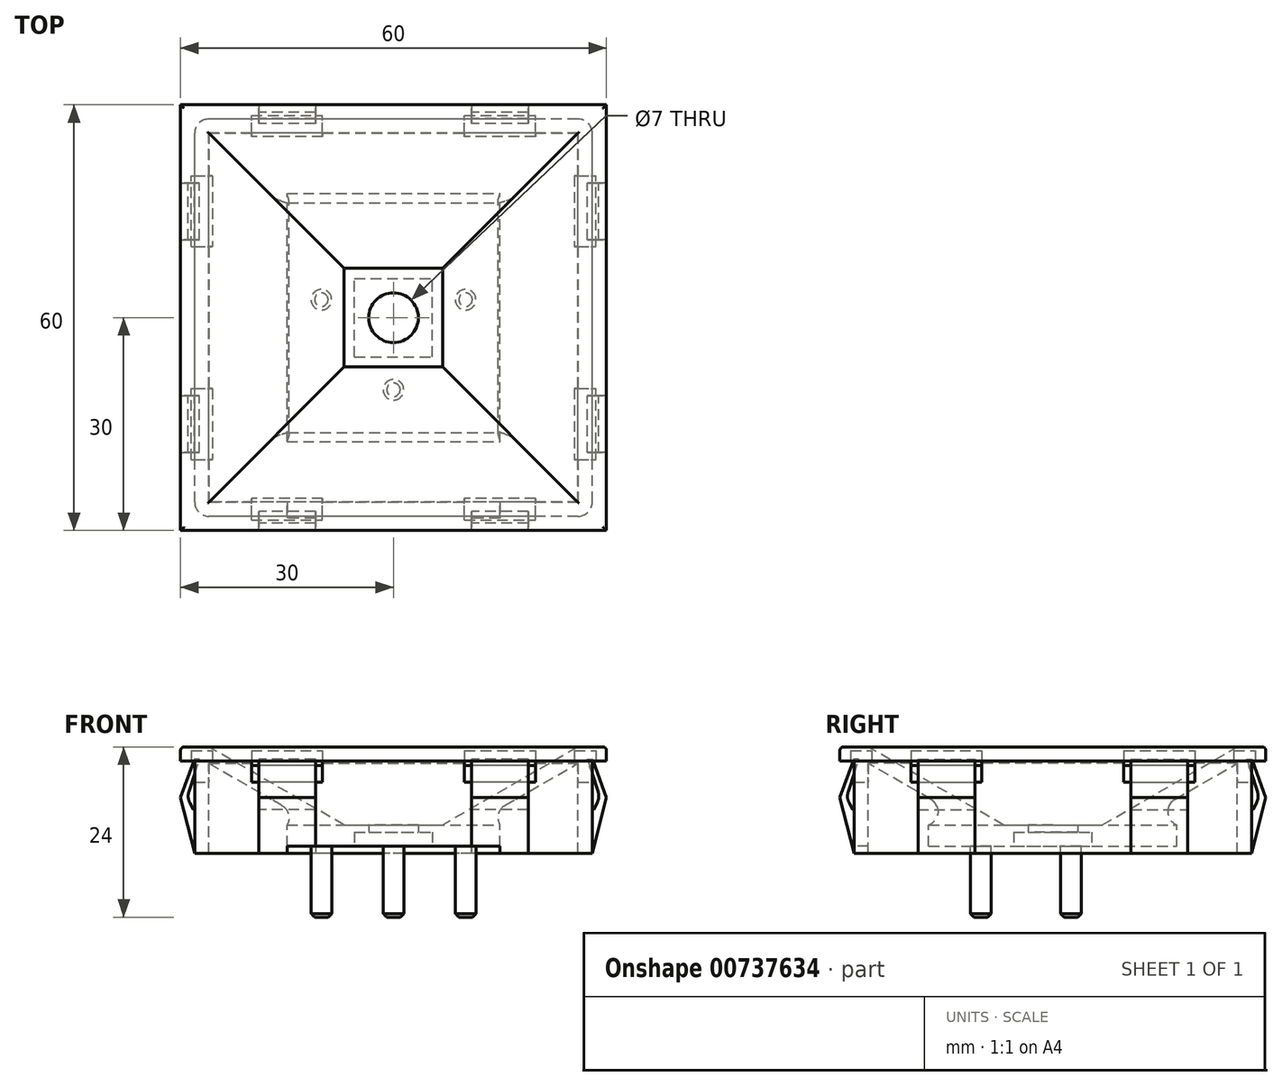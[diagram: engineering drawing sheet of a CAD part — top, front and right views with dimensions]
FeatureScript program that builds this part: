
annotation { "Feature Type Name" : "Feature", "Feature Type Description" : "" }
export const myFeature = defineFeature(function(context is Context, id is Id, definition is map)
    precondition{}
    {
        {
            var Q0;
            Q0=qCreatedBy(makeId("Top.planeOp"),FACE);
            var sketch = newSketch(context, id + "F0", { "sketchPlane" : qUnion([Q0])});
            skLineSegment(sketch, "E0.bottom", {"start": v(30, -30) * mm, "end": v(-30, -30) * mm});
            skLineSegment(sketch, "E0.top", {"start": v(30, 30) * mm, "end": v(-30, 30) * mm});
            skLineSegment(sketch, "E0.left", {"start": v(30, -30) * mm, "end": v(30, 30) * mm});
            skLineSegment(sketch, "E0.right", {"start": v(-30, -30) * mm, "end": v(-30, 30) * mm});
            skPoint(sketch, "E0.middle", {"position": v(0, 0) * mm});
            skSolve(sketch);
        }
        {
            var Q0;
            Q0=makeQuery(id+"F0.imprint","IMPRINT",FACE,{"disambiguationData":[TD([[makeQuery(id+"F0.imprint","IMPRINT",EDGE,{"derivedFrom":sQuery(id+"F0.wireOp",EDGE,"E0.bottom")}),-1.0]])]});
            extrude(context, id + "F1", {"entities" : qUnion([Q0]), "oppositeDirection" : true, "depth" : 13 * mm, "offsetDistance" : 25 * mm, "hasDraft" : true, "draftAngle" : 60 * degree, "draftPullDirection" : true});
        }
        {
            var Q0;
            Q0 = qSketchRegion(id + "F0", true);
            extrude(context, id + "F2", {"entities" : qUnion([Q0]), "operationType" : NewBodyOperationType.ADD, "oppositeDirection" : true, "depth" : 2 * mm, "offsetDistance" : 25 * mm});
        }
        {
            var Q0;
            Q0=makeQuery(id+"F1.opExtrude","CAP_FACE",FACE,{"disambiguationData":[OSD([sQuery(id+"F0.wireOp",EDGE,"E0.bottom"),sQuery(id+"F0.wireOp",EDGE,"E0.top"),sQuery(id+"F0.wireOp",EDGE,"E0.left"),sQuery(id+"F0.wireOp",EDGE,"E0.right")])],"isStart":true});
            shell(context, id + "F3", {"entities" : qUnion([Q0]), "thickness" : 2 * mm});
        }
        {
            var Q0;
            Q0=makeQuery(id+"F3.opShell","OFFSET_FACE",FACE,{"disambiguationData":[OSD([sQuery(id+"F0.wireOp",EDGE,"E0.bottom"),sQuery(id+"F0.wireOp",EDGE,"E0.top"),sQuery(id+"F0.wireOp",EDGE,"E0.left"),sQuery(id+"F0.wireOp",EDGE,"E0.right")])]});
            var sketch = newSketch(context, id + "F4", { "sketchPlane" : qUnion([Q0])});
            skLineSegment(sketch, "E1.bottom", {"start": v(-15, -17.5) * mm, "end": v(15, -17.5) * mm});
            skLineSegment(sketch, "E1.top", {"start": v(-15, 17.5) * mm, "end": v(15, 17.5) * mm});
            skLineSegment(sketch, "E1.left", {"start": v(-15, -17.5) * mm, "end": v(-15, 17.5) * mm});
            skLineSegment(sketch, "E1.right", {"start": v(15, -17.5) * mm, "end": v(15, 17.5) * mm});
            skPoint(sketch, "E1.middle", {"position": v(0, 0) * mm});
            skSolve(sketch);
        }
        {
            var Q0;
            Q0 = qSketchRegion(id + "F4", true);
            extrude(context, id + "F5", {"entities" : qUnion([Q0]), "operationType" : NewBodyOperationType.ADD, "oppositeDirection" : true, "depth" : 3 * mm, "offsetDistance" : 25 * mm});
        }
        {
            var Q0;
            Q0=makeQuery(id+"F5.boolean.opBoolean","INTERSECT",EDGE,{"derivedFrom":[makeQuery(id+"F1.opExtrude","SWEPT_FACE",FACE,{"disambiguationData":[OSD([sQuery(id+"F0.wireOp",EDGE,"E0.bottom")])]}),makeQuery(id+"F5.opExtrude","CAP_FACE",FACE,{"disambiguationData":[OSD([sQuery(id+"F4.wireOp",EDGE,"E1.bottom"),sQuery(id+"F4.wireOp",EDGE,"E1.top"),sQuery(id+"F4.wireOp",EDGE,"E1.left"),sQuery(id+"F4.wireOp",EDGE,"E1.right")])],"isStart":true})]});
            var Q1;
            Q1=makeQuery(id+"F5.boolean.opBoolean","INTERSECT",EDGE,{"derivedFrom":[makeQuery(id+"F1.opExtrude","SWEPT_FACE",FACE,{"disambiguationData":[OSD([sQuery(id+"F0.wireOp",EDGE,"E0.top")])]}),makeQuery(id+"F5.opExtrude","CAP_FACE",FACE,{"disambiguationData":[OSD([sQuery(id+"F4.wireOp",EDGE,"E1.bottom"),sQuery(id+"F4.wireOp",EDGE,"E1.top"),sQuery(id+"F4.wireOp",EDGE,"E1.left"),sQuery(id+"F4.wireOp",EDGE,"E1.right")])],"isStart":true})]});
            var Q2;
            Q2=makeQuery(id+"F5.boolean.opBoolean","INTERSECT",EDGE,{"derivedFrom":[makeQuery(id+"F1.opExtrude","SWEPT_FACE",FACE,{"disambiguationData":[OSD([sQuery(id+"F0.wireOp",EDGE,"E0.right")])]}),makeQuery(id+"F5.opExtrude","CAP_FACE",FACE,{"disambiguationData":[OSD([sQuery(id+"F4.wireOp",EDGE,"E1.bottom"),sQuery(id+"F4.wireOp",EDGE,"E1.top"),sQuery(id+"F4.wireOp",EDGE,"E1.left"),sQuery(id+"F4.wireOp",EDGE,"E1.right")])],"isStart":true})]});
            var Q3;
            Q3=makeQuery(id+"F5.boolean.opBoolean","INTERSECT",EDGE,{"derivedFrom":[makeQuery(id+"F1.opExtrude","SWEPT_FACE",FACE,{"disambiguationData":[OSD([sQuery(id+"F0.wireOp",EDGE,"E0.left")])]}),makeQuery(id+"F5.opExtrude","CAP_FACE",FACE,{"disambiguationData":[OSD([sQuery(id+"F4.wireOp",EDGE,"E1.bottom"),sQuery(id+"F4.wireOp",EDGE,"E1.top"),sQuery(id+"F4.wireOp",EDGE,"E1.left"),sQuery(id+"F4.wireOp",EDGE,"E1.right")])],"isStart":true})]});
            fillet(context, id + "F6", {"entities" : qUnion([Q0, Q1, Q2, Q3]), "radius" : 2 * mm, "tangentPropagation" : true, "allowEdgeOverflow" : false});
        }
        {
            var Q0;
            Q0=makeQuery(id+"F5.opExtrude","CAP_FACE",FACE,{"disambiguationData":[OSD([sQuery(id+"F4.wireOp",EDGE,"E1.bottom"),sQuery(id+"F4.wireOp",EDGE,"E1.top"),sQuery(id+"F4.wireOp",EDGE,"E1.left"),sQuery(id+"F4.wireOp",EDGE,"E1.right")])],"isStart":false});
            var sketch = newSketch(context, id + "F7", { "sketchPlane" : qUnion([Q0])});
            skLineSegment(sketch, "E2.bottom", {"start": v(-5.5, 5.5) * mm, "end": v(5.5, 5.5) * mm});
            skLineSegment(sketch, "E2.top", {"start": v(-5.5, -5.5) * mm, "end": v(5.5, -5.5) * mm});
            skLineSegment(sketch, "E2.left", {"start": v(-5.5, 5.5) * mm, "end": v(-5.5, -5.5) * mm});
            skLineSegment(sketch, "E2.right", {"start": v(5.5, 5.5) * mm, "end": v(5.5, -5.5) * mm});
            skPoint(sketch, "E2.middle", {"position": v(0, 0) * mm});
            skCircle(sketch, "E3", {"center": v(0, 0) * mm, "radius": 3.5 * mm});
            skSolve(sketch);
        }
        {
            var Q0;
            Q0=makeQuery(id+"F7.imprint","IMPRINT",FACE,{"disambiguationData":[TD([[makeQuery(id+"F7.imprint","IMPRINT",EDGE,{"derivedFrom":sQuery(id+"F7.wireOp",EDGE,"E2.bottom")}),-1.0]])]});
            extrude(context, id + "F8", {"entities" : qUnion([Q0]), "operationType" : NewBodyOperationType.REMOVE, "oppositeDirection" : true, "depth" : 2 * mm, "offsetDistance" : 25 * mm});
        }
        {
            var Q0;
            Q0=makeQuery(id+"F8.boolean.opBoolean","SPLIT",FACE,{"disambiguationData":[TD([makeQuery(id+"F8.opExtrude","SWEPT_FACE",FACE,{"disambiguationData":[OSD([sQuery(id+"F7.wireOp",EDGE,"E3")])]})])],"derivedFrom":makeQuery(id+"F5.opExtrude","CAP_FACE",FACE,{"disambiguationData":[OSD([sQuery(id+"F4.wireOp",EDGE,"E1.bottom"),sQuery(id+"F4.wireOp",EDGE,"E1.top"),sQuery(id+"F4.wireOp",EDGE,"E1.left"),sQuery(id+"F4.wireOp",EDGE,"E1.right")])],"isStart":false})});
            extrude(context, id + "F9", {"entities" : qUnion([Q0]), "operationType" : NewBodyOperationType.REMOVE, "endBound" : BoundingType.THROUGH_ALL, "oppositeDirection" : true, "depth" : 25 * mm, "offsetDistance" : 25 * mm});
        }
        {
            var Q0;
            {var subQ0=sQuery(id+"F4.wireOp",EDGE,"E1.left");var subQ1=sQuery(id+"F4.wireOp",EDGE,"E1.top");var subQ2=sQuery(id+"F4.wireOp",EDGE,"E1.right");var subQ3=sQuery(id+"F4.wireOp",EDGE,"E1.bottom");Q0=makeQuery(id+"F8.boolean.opBoolean","SPLIT",FACE,{"disambiguationData":[TD([makeQuery(id+"F5.opExtrude","SWEPT_FACE",FACE,{"disambiguationData":[OSD([subQ3])]})])],"derivedFrom":makeQuery(id+"F5.opExtrude","CAP_FACE",FACE,{"disambiguationData":[OSD([subQ3,subQ1,subQ0,subQ2])],"isStart":false})});}
            var sketch = newSketch(context, id + "F10", { "sketchPlane" : qUnion([Q0])});
            skCircle(sketch, "E4", {"center": v(-10.16, -2.54) * mm, "radius": 1.45 * mm});
            skCircle(sketch, "E5", {"center": v(0, 10.16) * mm, "radius": 1.45 * mm});
            skCircle(sketch, "E6", {"center": v(10.16, -2.54) * mm, "radius": 1.45 * mm});
            skSolve(sketch);
        }
        {
            var Q0;
            Q0 = qSketchRegion(id + "F10", true);
            extrude(context, id + "F11", {"entities" : qUnion([Q0]), "operationType" : NewBodyOperationType.ADD, "depth" : 10 * mm, "offsetDistance" : 25 * mm});
        }
        {
            var Q0;
            Q0=makeQuery(id+"F11.opExtrude","CAP_EDGE",EDGE,{"disambiguationData":[OSD([sQuery(id+"F10.wireOp",EDGE,"E6")])],"isStart":false});
            var Q1;
            Q1=makeQuery(id+"F11.opExtrude","CAP_EDGE",EDGE,{"disambiguationData":[OSD([sQuery(id+"F10.wireOp",EDGE,"E4")])],"isStart":false});
            var Q2;
            Q2=makeQuery(id+"F11.opExtrude","CAP_EDGE",EDGE,{"disambiguationData":[OSD([sQuery(id+"F10.wireOp",EDGE,"E5")])],"isStart":false});
            chamfer(context, id + "F12", {"entities" : qUnion([Q0, Q1, Q2]), "width" : 0.5 * mm, "tangentPropagation" : true});
        }
        {
            var Q0;
            Q0=makeQuery(id+"F1.opExtrude","CAP_FACE",FACE,{"disambiguationData":[OSD([sQuery(id+"F0.wireOp",EDGE,"E0.bottom"),sQuery(id+"F0.wireOp",EDGE,"E0.top"),sQuery(id+"F0.wireOp",EDGE,"E0.left"),sQuery(id+"F0.wireOp",EDGE,"E0.right")])],"isStart":true});
            fillet(context, id + "F13", {"entities" : qUnion([Q0]), "radius" : 0.5 * mm, "tangentPropagation" : true, "allowEdgeOverflow" : false});
        }
        {
            var Q0;
            Q0=makeQuery(id+"F2.opExtrude","CAP_FACE",FACE,{"disambiguationData":[OSD([sQuery(id+"F0.wireOp",EDGE,"E0.bottom"),sQuery(id+"F0.wireOp",EDGE,"E0.top"),sQuery(id+"F0.wireOp",EDGE,"E0.left"),sQuery(id+"F0.wireOp",EDGE,"E0.right")])],"isStart":false});
            var sketch = newSketch(context, id + "F14", { "sketchPlane" : qUnion([Q0])});
            skLineSegment(sketch, "E7.bottom", {"start": v(25.5, -10) * mm, "end": v(28.5, -10) * mm});
            skLineSegment(sketch, "E7.top", {"start": v(25.5, -20) * mm, "end": v(28.5, -20) * mm});
            skLineSegment(sketch, "E7.left", {"start": v(25.5, -10) * mm, "end": v(25.5, -20) * mm});
            skLineSegment(sketch, "E7.right", {"start": v(28.5, -10) * mm, "end": v(28.5, -20) * mm});
            skPoint(sketch, "E7.middle", {"position": v(27, -15) * mm});
            skLineSegment(sketch, "E8.0.1.0", {"start": v(28.5, 20) * mm, "end": v(28.5, 10) * mm});
            skPoint(sketch, "E8.0.1.1", {"position": v(27, 15) * mm});
            skLineSegment(sketch, "E8.0.1.2", {"start": v(25.5, 10) * mm, "end": v(28.5, 10) * mm});
            skLineSegment(sketch, "E8.0.1.3", {"start": v(25.5, 20) * mm, "end": v(25.5, 10) * mm});
            skLineSegment(sketch, "E8.0.1.4", {"start": v(25.5, 20) * mm, "end": v(28.5, 20) * mm});
            skLineSegment(sketch, "E8.1.0.0", {"start": v(-25.5, -10) * mm, "end": v(-25.5, -20) * mm});
            skPoint(sketch, "E8.1.0.1", {"position": v(-27, -15) * mm});
            skLineSegment(sketch, "E8.1.0.2", {"start": v(-28.5, -20) * mm, "end": v(-25.5, -20) * mm});
            skLineSegment(sketch, "E8.1.0.3", {"start": v(-28.5, -10) * mm, "end": v(-28.5, -20) * mm});
            skLineSegment(sketch, "E8.1.0.4", {"start": v(-28.5, -10) * mm, "end": v(-25.5, -10) * mm});
            skLineSegment(sketch, "E8.1.1.0", {"start": v(-25.5, 20) * mm, "end": v(-25.5, 10) * mm});
            skPoint(sketch, "E8.1.1.1", {"position": v(-27, 15) * mm});
            skLineSegment(sketch, "E8.1.1.2", {"start": v(-28.5, 10) * mm, "end": v(-25.5, 10) * mm});
            skLineSegment(sketch, "E8.1.1.3", {"start": v(-28.5, 20) * mm, "end": v(-28.5, 10) * mm});
            skLineSegment(sketch, "E8.1.1.4", {"start": v(-28.5, 20) * mm, "end": v(-25.5, 20) * mm});
            skLineSegment(sketch, "E8.direction1", {"start": v(28.5, -20) * mm, "end": v(-25.5, -20) * mm, "construction": true});
            skLineSegment(sketch, "E8.direction2", {"start": v(28.5, -20) * mm, "end": v(28.5, 10) * mm, "construction": true});
            skLineSegment(sketch, "E9.bottom", {"start": v(10, -25.5) * mm, "end": v(20, -25.5) * mm});
            skLineSegment(sketch, "E9.top", {"start": v(10, -28.5) * mm, "end": v(20, -28.5) * mm});
            skLineSegment(sketch, "E9.left", {"start": v(10, -25.5) * mm, "end": v(10, -28.5) * mm});
            skLineSegment(sketch, "E9.right", {"start": v(20, -25.5) * mm, "end": v(20, -28.5) * mm});
            skPoint(sketch, "E9.middle", {"position": v(15, -27) * mm});
            skPoint(sketch, "E10.0.1.0", {"position": v(15, 27) * mm});
            skLineSegment(sketch, "E10.0.1.1", {"start": v(10, 28.5) * mm, "end": v(10, 25.5) * mm});
            skLineSegment(sketch, "E10.0.1.2", {"start": v(10, 25.5) * mm, "end": v(20, 25.5) * mm});
            skLineSegment(sketch, "E10.0.1.3", {"start": v(20, 28.5) * mm, "end": v(20, 25.5) * mm});
            skLineSegment(sketch, "E10.0.1.4", {"start": v(10, 28.5) * mm, "end": v(20, 28.5) * mm});
            skPoint(sketch, "E10.1.0.0", {"position": v(-15, -27) * mm});
            skLineSegment(sketch, "E10.1.0.1", {"start": v(-20, -25.5) * mm, "end": v(-20, -28.5) * mm});
            skLineSegment(sketch, "E10.1.0.2", {"start": v(-20, -28.5) * mm, "end": v(-10, -28.5) * mm});
            skLineSegment(sketch, "E10.1.0.3", {"start": v(-10, -25.5) * mm, "end": v(-10, -28.5) * mm});
            skLineSegment(sketch, "E10.1.0.4", {"start": v(-20, -25.5) * mm, "end": v(-10, -25.5) * mm});
            skPoint(sketch, "E10.1.1.0", {"position": v(-15, 27) * mm});
            skLineSegment(sketch, "E10.1.1.1", {"start": v(-20, 28.5) * mm, "end": v(-20, 25.5) * mm});
            skLineSegment(sketch, "E10.1.1.2", {"start": v(-20, 25.5) * mm, "end": v(-10, 25.5) * mm});
            skLineSegment(sketch, "E10.1.1.3", {"start": v(-10, 28.5) * mm, "end": v(-10, 25.5) * mm});
            skLineSegment(sketch, "E10.1.1.4", {"start": v(-20, 28.5) * mm, "end": v(-10, 28.5) * mm});
            skLineSegment(sketch, "E10.direction1", {"start": v(15, -27) * mm, "end": v(-15, -27) * mm, "construction": true});
            skLineSegment(sketch, "E10.direction2", {"start": v(15, -27) * mm, "end": v(15, 27) * mm, "construction": true});
            skSolve(sketch);
        }
        {
            var Q0;
            {var subQ24=sQuery(id+"F14.wireOp",EDGE,"E7.right");Q0=makeQuery(id+"F14.imprint","IMPRINT",FACE,{"disambiguationData":[TD([[makeQuery(id+"F14.imprint","IMPRINT",EDGE,{"derivedFrom":subQ24}),1.0]])]});}
            var sketch = newSketch(context, id + "F15", { "sketchPlane" : qUnion([Q0])});
            skLineSegment(sketch, "E11.0", {"start": v(26, -28) * mm, "end": v(-26, -28) * mm});
            skLineSegment(sketch, "E11.1", {"start": v(28, 26) * mm, "end": v(28, -26) * mm});
            skLineSegment(sketch, "E11.2", {"start": v(26, 28) * mm, "end": v(-26, 28) * mm});
            skLineSegment(sketch, "E11.3", {"start": v(-28, 26) * mm, "end": v(-28, -26) * mm});
            skLineSegment(sketch, "E12.0", {"start": v(26, -26) * mm, "end": v(-26, -26) * mm});
            skLineSegment(sketch, "E12.1", {"start": v(26, 26) * mm, "end": v(26, -26) * mm});
            skLineSegment(sketch, "E12.2", {"start": v(26, 26) * mm, "end": v(-26, 26) * mm});
            skLineSegment(sketch, "E12.3", {"start": v(-26, 26) * mm, "end": v(-26, -26) * mm});
            skPoint(sketch, "E13.visualSharp", {"position": v(28, -28) * mm});
            skArc(sketch, "E13.filletArc", {"start": v(26, -28) * mm, "mid": v(27.41, -27.41) * mm, "end": v(28, -26) * mm});
            skPoint(sketch, "E14.visualSharp", {"position": v(-28, -28) * mm});
            skArc(sketch, "E14.filletArc", {"start": v(-28, -26) * mm, "mid": v(-27.41, -27.41) * mm, "end": v(-26, -28) * mm});
            skPoint(sketch, "E15.visualSharp", {"position": v(-28, 28) * mm});
            skArc(sketch, "E15.filletArc", {"start": v(-26, 28) * mm, "mid": v(-27.41, 27.41) * mm, "end": v(-28, 26) * mm});
            skPoint(sketch, "E16.visualSharp", {"position": v(28, 28) * mm});
            skArc(sketch, "E16.filletArc", {"start": v(28, 26) * mm, "mid": v(27.41, 27.41) * mm, "end": v(26, 28) * mm});
            skSolve(sketch);
        }
        {
            var Q0;
            Q0 = qSketchRegion(id + "F15", true);
            extrude(context, id + "F16", {"entities" : qUnion([Q0]), "operationType" : NewBodyOperationType.ADD, "depth" : 13 * mm, "offsetDistance" : 25 * mm});
        }
        {
            var Q0;
            Q0 = qSketchRegion(id + "F14", true);
            extrude(context, id + "F17", {"entities" : qUnion([Q0]), "operationType" : NewBodyOperationType.REMOVE, "oppositeDirection" : true, "depth" : 1.5 * mm, "offsetDistance" : 25 * mm});
        }
        {
            var Q0;
            Q0 = qSketchRegion(id + "F14", true);
            extrude(context, id + "F18", {"entities" : qUnion([Q0]), "operationType" : NewBodyOperationType.REMOVE, "depth" : 3 * mm, "offsetDistance" : 25 * mm});
        }
        {
            var Q0;
            Q0=qCreatedBy(makeId("Front.planeOp"),FACE);
            var Q1;
            Q1=sQuery(id+"F14.wireOp",VERTEX,"E7.middle");
            cPlane(context, id + "F19", {"entities" : qUnion([Q0, Q1]), "cplaneType" : CPlaneType.PLANE_POINT, "offset" : 25 * mm, "width" : 150 * mm, "height" : 150 * mm});
        }
        {
            var Q0;
            Q0=qCreatedBy(id+"F19.planeOp",FACE);
            var sketch = newSketch(context, id + "F20", { "sketchPlane" : qUnion([Q0])});
            skLineSegment(sketch, "E17", {"start": v(28.04, -1.74) * mm, "end": v(30, -7.16) * mm});
            skLineSegment(sketch, "E18", {"start": v(30, -7.16) * mm, "end": v(28, -15) * mm});
            skLineSegment(sketch, "E19", {"start": v(28, -15) * mm, "end": v(26.25, -15) * mm});
            skLineSegment(sketch, "E20", {"start": v(26.25, -15) * mm, "end": v(26.25, -7.77) * mm});
            skLineSegment(sketch, "E21", {"start": v(26.25, -7.77) * mm, "end": v(28, -7.77) * mm});
            skLineSegment(sketch, "E22", {"start": v(28, -7.77) * mm, "end": v(28, -8.78) * mm});
            skLineSegment(sketch, "E23", {"start": v(28.19, -8.83) * mm, "end": v(28.69, -7.92) * mm});
            skLineSegment(sketch, "E24", {"start": v(28.83, -6.34) * mm, "end": v(27.34, -1.74) * mm});
            skLineSegment(sketch, "E25", {"start": v(27.34, -1.74) * mm, "end": v(28.04, -1.74) * mm});
            skPoint(sketch, "E26.visualSharp", {"position": v(28, -9.17) * mm});
            skArc(sketch, "E26.filletArc", {"start": v(28, -8.78) * mm, "mid": v(28.08, -8.88) * mm, "end": v(28.19, -8.83) * mm});
            skLineSegment(sketch, "E27", {"start": v(30, -2) * mm, "end": v(30, -15) * mm, "construction": true});
            skLineSegment(sketch, "E28", {"start": v(30, -15) * mm, "end": v(28, -15) * mm, "construction": true});
            skPoint(sketch, "E29.visualSharp", {"position": v(29.1, -7.16) * mm});
            skArc(sketch, "E29.filletArc", {"start": v(28.69, -7.92) * mm, "mid": v(28.92, -7.14) * mm, "end": v(28.83, -6.34) * mm});
            skLineSegment(sketch, "E30.MirrorCS", {"start": v(-28, -15) * mm, "end": v(-26.25, -15) * mm});
            skLineSegment(sketch, "E31.MirrorCS", {"start": v(-26.25, -15) * mm, "end": v(-26.25, -7.77) * mm});
            skLineSegment(sketch, "E32.MirrorCS", {"start": v(-26.25, -7.77) * mm, "end": v(-28, -7.77) * mm});
            skLineSegment(sketch, "E33.MirrorCS", {"start": v(-28, -7.77) * mm, "end": v(-28, -8.78) * mm});
            skArc(sketch, "E34.MirrorCS", {"start": v(-28, -8.78) * mm, "mid": v(-28.08, -8.88) * mm, "end": v(-28.19, -8.83) * mm});
            skLineSegment(sketch, "E35.MirrorCS", {"start": v(-28.19, -8.83) * mm, "end": v(-28.69, -7.92) * mm});
            skArc(sketch, "E36.MirrorCS", {"start": v(-28.69, -7.92) * mm, "mid": v(-28.92, -7.14) * mm, "end": v(-28.83, -6.34) * mm});
            skLineSegment(sketch, "E37.MirrorCS", {"start": v(-28.83, -6.34) * mm, "end": v(-27.34, -1.74) * mm});
            skLineSegment(sketch, "E38.MirrorCS", {"start": v(-27.34, -1.74) * mm, "end": v(-28.04, -1.74) * mm});
            skLineSegment(sketch, "E39.MirrorCS", {"start": v(-28.04, -1.74) * mm, "end": v(-30, -7.16) * mm});
            skLineSegment(sketch, "E40.MirrorCS", {"start": v(-30, -7.16) * mm, "end": v(-28, -15) * mm});
            skSolve(sketch);
        }
        {
            var Q0;
            Q0 = qSketchRegion(id + "F20", true);
            extrude(context, id + "F21", {"entities" : qUnion([Q0]), "operationType" : NewBodyOperationType.ADD, "endBound" : BoundingType.SYMMETRIC, "depth" : 8 * mm, "offsetDistance" : 25 * mm});
        }
        {
            var Q0;
            Q0=qCreatedBy(makeId("Front.planeOp"),FACE);
            var Q1;
            Q1=sQuery(id+"F14.wireOp",VERTEX,"E8.0.1.1");
            cPlane(context, id + "F22", {"entities" : qUnion([Q0, Q1]), "cplaneType" : CPlaneType.PLANE_POINT, "offset" : 25 * mm, "width" : 150 * mm, "height" : 150 * mm});
        }
        {
            var Q0;
            Q0=qCreatedBy(id+"F22.planeOp",FACE);
            var sketch = newSketch(context, id + "F23", { "sketchPlane" : qUnion([Q0])});
            skArc(sketch, "E41.0.0", {"start": v(28.83, -6.34) * mm, "mid": v(28.92, -7.14) * mm, "end": v(28.69, -7.92) * mm});
            skLineSegment(sketch, "E41.0.1", {"start": v(28.69, -7.92) * mm, "end": v(28.19, -8.83) * mm});
            skArc(sketch, "E41.0.2", {"start": v(28.19, -8.83) * mm, "mid": v(28.08, -8.88) * mm, "end": v(28, -8.78) * mm});
            skLineSegment(sketch, "E41.0.3", {"start": v(28, -8.78) * mm, "end": v(28, -7.77) * mm});
            skLineSegment(sketch, "E41.0.4", {"start": v(28, -7.77) * mm, "end": v(26.25, -7.77) * mm});
            skLineSegment(sketch, "E41.0.5", {"start": v(26.25, -7.77) * mm, "end": v(26.25, -15) * mm});
            skLineSegment(sketch, "E41.0.6", {"start": v(26.25, -15) * mm, "end": v(28, -15) * mm});
            skLineSegment(sketch, "E41.0.7", {"start": v(28, -15) * mm, "end": v(30, -7.16) * mm});
            skLineSegment(sketch, "E41.0.8", {"start": v(30, -7.16) * mm, "end": v(28.04, -1.74) * mm});
            skLineSegment(sketch, "E41.0.9", {"start": v(28.04, -1.74) * mm, "end": v(27.34, -1.74) * mm});
            skLineSegment(sketch, "E41.0.10", {"start": v(27.34, -1.74) * mm, "end": v(28.83, -6.34) * mm});
            skLineSegment(sketch, "E41.1.0", {"start": v(-30, -7.16) * mm, "end": v(-28, -15) * mm});
            skLineSegment(sketch, "E41.1.1", {"start": v(-28, -15) * mm, "end": v(-26.25, -15) * mm});
            skLineSegment(sketch, "E41.1.2", {"start": v(-26.25, -15) * mm, "end": v(-26.25, -7.77) * mm});
            skLineSegment(sketch, "E41.1.3", {"start": v(-26.25, -7.77) * mm, "end": v(-28, -7.77) * mm});
            skLineSegment(sketch, "E41.1.4", {"start": v(-28, -7.77) * mm, "end": v(-28, -8.78) * mm});
            skArc(sketch, "E41.1.5", {"start": v(-28, -8.78) * mm, "mid": v(-28.08, -8.88) * mm, "end": v(-28.19, -8.83) * mm});
            skLineSegment(sketch, "E41.1.6", {"start": v(-28.19, -8.83) * mm, "end": v(-28.69, -7.92) * mm});
            skArc(sketch, "E41.1.7", {"start": v(-28.69, -7.92) * mm, "mid": v(-28.92, -7.14) * mm, "end": v(-28.83, -6.34) * mm});
            skLineSegment(sketch, "E41.1.8", {"start": v(-28.83, -6.34) * mm, "end": v(-27.34, -1.74) * mm});
            skLineSegment(sketch, "E41.1.9", {"start": v(-27.34, -1.74) * mm, "end": v(-28.04, -1.74) * mm});
            skLineSegment(sketch, "E41.1.10", {"start": v(-28.04, -1.74) * mm, "end": v(-30, -7.16) * mm});
            skSolve(sketch);
        }
        {
            var Q0;
            Q0 = qSketchRegion(id + "F23", true);
            extrude(context, id + "F24", {"entities" : qUnion([Q0]), "operationType" : NewBodyOperationType.ADD, "endBound" : BoundingType.SYMMETRIC, "depth" : 8 * mm, "offsetDistance" : 25 * mm});
        }
        {
            var Q0;
            Q0=qCreatedBy(makeId("Right.planeOp"),FACE);
            var Q1;
            Q1=sQuery(id+"F14.wireOp",VERTEX,"E10.1.1.0");
            cPlane(context, id + "F25", {"entities" : qUnion([Q0, Q1]), "cplaneType" : CPlaneType.PLANE_POINT, "offset" : 25 * mm, "width" : 150 * mm, "height" : 150 * mm});
        }
        {
            var Q0;
            Q0=qCreatedBy(id+"F25.planeOp",FACE);
            var sketch = newSketch(context, id + "F26", { "sketchPlane" : qUnion([Q0])});
            skLineSegment(sketch, "E42", {"start": v(28.04, -1.74) * mm, "end": v(30, -7.16) * mm});
            skLineSegment(sketch, "E43", {"start": v(30, -7.16) * mm, "end": v(28, -15) * mm});
            skLineSegment(sketch, "E44", {"start": v(28, -15) * mm, "end": v(26.25, -15) * mm});
            skLineSegment(sketch, "E45", {"start": v(26.25, -15) * mm, "end": v(26.25, -7.77) * mm});
            skLineSegment(sketch, "E46", {"start": v(26.25, -7.77) * mm, "end": v(28, -7.77) * mm});
            skLineSegment(sketch, "E47", {"start": v(28, -7.77) * mm, "end": v(28, -8.78) * mm});
            skLineSegment(sketch, "E48", {"start": v(28.19, -8.83) * mm, "end": v(28.69, -7.92) * mm});
            skLineSegment(sketch, "E49", {"start": v(28.83, -6.34) * mm, "end": v(27.34, -1.74) * mm});
            skLineSegment(sketch, "E50", {"start": v(27.34, -1.74) * mm, "end": v(28.04, -1.74) * mm});
            skPoint(sketch, "E51.visualSharp", {"position": v(28, -9.17) * mm});
            skArc(sketch, "E51.filletArc", {"start": v(28, -8.78) * mm, "mid": v(28.08, -8.88) * mm, "end": v(28.19, -8.83) * mm});
            skPoint(sketch, "E52.visualSharp", {"position": v(29.1, -7.16) * mm});
            skArc(sketch, "E52.filletArc", {"start": v(28.69, -7.92) * mm, "mid": v(28.92, -7.14) * mm, "end": v(28.83, -6.34) * mm});
            skLineSegment(sketch, "E53.MirrorCS", {"start": v(-30, -7.16) * mm, "end": v(-28, -15) * mm});
            skLineSegment(sketch, "E54.MirrorCS", {"start": v(-28, -15) * mm, "end": v(-26.25, -15) * mm});
            skLineSegment(sketch, "E55.MirrorCS", {"start": v(-26.25, -15) * mm, "end": v(-26.25, -7.77) * mm});
            skLineSegment(sketch, "E56.MirrorCS", {"start": v(-26.25, -7.77) * mm, "end": v(-28, -7.77) * mm});
            skLineSegment(sketch, "E57.MirrorCS", {"start": v(-28, -7.77) * mm, "end": v(-28, -8.78) * mm});
            skArc(sketch, "E58.MirrorCS", {"start": v(-28, -8.78) * mm, "mid": v(-28.08, -8.88) * mm, "end": v(-28.19, -8.83) * mm});
            skLineSegment(sketch, "E59.MirrorCS", {"start": v(-28.19, -8.83) * mm, "end": v(-28.69, -7.92) * mm});
            skArc(sketch, "E60.MirrorCS", {"start": v(-28.69, -7.92) * mm, "mid": v(-28.92, -7.14) * mm, "end": v(-28.83, -6.34) * mm});
            skLineSegment(sketch, "E61.MirrorCS", {"start": v(-28.83, -6.34) * mm, "end": v(-27.34, -1.74) * mm});
            skLineSegment(sketch, "E62.MirrorCS", {"start": v(-27.34, -1.74) * mm, "end": v(-28.04, -1.74) * mm});
            skLineSegment(sketch, "E63.MirrorCS", {"start": v(-28.04, -1.74) * mm, "end": v(-30, -7.16) * mm});
            skSolve(sketch);
        }
        {
            var Q0;
            Q0 = qSketchRegion(id + "F26", true);
            extrude(context, id + "F27", {"entities" : qUnion([Q0]), "operationType" : NewBodyOperationType.ADD, "endBound" : BoundingType.SYMMETRIC, "depth" : 8 * mm, "offsetDistance" : 25 * mm});
        }
        {
            var Q0;
            Q0=qCreatedBy(makeId("Right.planeOp"),FACE);
            var Q1;
            Q1=sQuery(id+"F14.wireOp",VERTEX,"E9.middle");
            cPlane(context, id + "F28", {"entities" : qUnion([Q0, Q1]), "cplaneType" : CPlaneType.PLANE_POINT, "offset" : 25 * mm, "width" : 150 * mm, "height" : 150 * mm});
        }
        {
            var Q0;
            Q0=qCreatedBy(id+"F28.planeOp",FACE);
            var sketch = newSketch(context, id + "F29", { "sketchPlane" : qUnion([Q0])});
            skArc(sketch, "E64.0.0", {"start": v(28.83, -6.34) * mm, "mid": v(28.92, -7.14) * mm, "end": v(28.69, -7.92) * mm});
            skLineSegment(sketch, "E64.0.1", {"start": v(28.69, -7.92) * mm, "end": v(28.19, -8.83) * mm});
            skArc(sketch, "E64.0.2", {"start": v(28.19, -8.83) * mm, "mid": v(28.08, -8.88) * mm, "end": v(28, -8.78) * mm});
            skLineSegment(sketch, "E64.0.3", {"start": v(28, -8.78) * mm, "end": v(28, -7.77) * mm});
            skLineSegment(sketch, "E64.0.4", {"start": v(28, -7.77) * mm, "end": v(26.25, -7.77) * mm});
            skLineSegment(sketch, "E64.0.5", {"start": v(26.25, -7.77) * mm, "end": v(26.25, -15) * mm});
            skLineSegment(sketch, "E64.0.6", {"start": v(26.25, -15) * mm, "end": v(28, -15) * mm});
            skLineSegment(sketch, "E64.0.7", {"start": v(28, -15) * mm, "end": v(30, -7.16) * mm});
            skLineSegment(sketch, "E64.0.8", {"start": v(30, -7.16) * mm, "end": v(28.04, -1.74) * mm});
            skLineSegment(sketch, "E64.0.9", {"start": v(28.04, -1.74) * mm, "end": v(27.34, -1.74) * mm});
            skLineSegment(sketch, "E64.0.10", {"start": v(27.34, -1.74) * mm, "end": v(28.83, -6.34) * mm});
            skLineSegment(sketch, "E64.1.0", {"start": v(-28.04, -1.74) * mm, "end": v(-30, -7.16) * mm});
            skLineSegment(sketch, "E64.1.1", {"start": v(-30, -7.16) * mm, "end": v(-28, -15) * mm});
            skLineSegment(sketch, "E64.1.2", {"start": v(-28, -15) * mm, "end": v(-26.25, -15) * mm});
            skLineSegment(sketch, "E64.1.3", {"start": v(-26.25, -15) * mm, "end": v(-26.25, -7.77) * mm});
            skLineSegment(sketch, "E64.1.4", {"start": v(-26.25, -7.77) * mm, "end": v(-28, -7.77) * mm});
            skLineSegment(sketch, "E64.1.5", {"start": v(-28, -7.77) * mm, "end": v(-28, -8.78) * mm});
            skArc(sketch, "E64.1.6", {"start": v(-28, -8.78) * mm, "mid": v(-28.08, -8.88) * mm, "end": v(-28.19, -8.83) * mm});
            skLineSegment(sketch, "E64.1.7", {"start": v(-28.19, -8.83) * mm, "end": v(-28.69, -7.92) * mm});
            skArc(sketch, "E64.1.8", {"start": v(-28.69, -7.92) * mm, "mid": v(-28.92, -7.14) * mm, "end": v(-28.83, -6.34) * mm});
            skLineSegment(sketch, "E64.1.9", {"start": v(-28.83, -6.34) * mm, "end": v(-27.34, -1.74) * mm});
            skLineSegment(sketch, "E64.1.10", {"start": v(-27.34, -1.74) * mm, "end": v(-28.04, -1.74) * mm});
            skSolve(sketch);
        }
        {
            var Q0;
            Q0 = qSketchRegion(id + "F29", true);
            extrude(context, id + "F30", {"entities" : qUnion([Q0]), "operationType" : NewBodyOperationType.ADD, "endBound" : BoundingType.SYMMETRIC, "depth" : 8 * mm, "offsetDistance" : 25 * mm});
        }
        {
            var Q0;
            {var subQ0=sQuery(id+"F4.wireOp",EDGE,"E1.left");var subQ1=sQuery(id+"F4.wireOp",EDGE,"E1.top");var subQ2=sQuery(id+"F4.wireOp",EDGE,"E1.right");var subQ3=sQuery(id+"F4.wireOp",EDGE,"E1.bottom");Q0=makeQuery(id+"F8.boolean.opBoolean","SPLIT",FACE,{"disambiguationData":[TD([makeQuery(id+"F5.opExtrude","SWEPT_FACE",FACE,{"disambiguationData":[OSD([subQ3])]})])],"derivedFrom":makeQuery(id+"F5.opExtrude","CAP_FACE",FACE,{"disambiguationData":[OSD([subQ3,subQ1,subQ0,subQ2])],"isStart":false})});}
            var sketch = newSketch(context, id + "F31", { "sketchPlane" : qUnion([Q0])});
            skLineSegment(sketch, "E65.bottom", {"start": v(15, 17.5) * mm, "end": v(-15, 17.5) * mm});
            skLineSegment(sketch, "E65.top", {"start": v(15, 30) * mm, "end": v(-15, 30) * mm});
            skLineSegment(sketch, "E65.left", {"start": v(15, 17.5) * mm, "end": v(15, 30) * mm});
            skLineSegment(sketch, "E65.right", {"start": v(-15, 17.5) * mm, "end": v(-15, 30) * mm});
            skSolve(sketch);
        }
        {
            var Q0;
            Q0 = qSketchRegion(id + "F31", true);
            extrude(context, id + "F32", {"entities" : qUnion([Q0]), "operationType" : NewBodyOperationType.REMOVE, "endBound" : BoundingType.THROUGH_ALL, "depth" : 25 * mm, "offsetDistance" : 25 * mm});
        }
    });
